# Revit family: Hager-Orion_Plus-IP65-D160-Cl.I-Steel_encl-630A-CH-de
name_source: partatom
category: Electrical Equipment
units: mm (PartAtom-declared; Revit-internal decimal feet)

## family parameters
Cut with Voids When Loaded = No
Host = Face
Panel Configuration = Two Columns, Circuits Across
Part Type = Panelboard
Room Calculation Point = No
Round Connector Dimension = Use Diameter
Shared = No

## types (14) — shared parameters
EF000003 - Montageart = EV000384 - Aufputz
EF000007 - Farbe = EV000270 - grau
EF000049 - Tiefe = 160 mm  [stored 0.524934 ft]
EF000116 - RAL-Nummer = 7035
EF000118 - Mit Montageplatte = No
EF000437 - Anzahl der Leitungseinführungen = 2
EF001596 - Werkstoff des Gehäuses = EV000179 - Stahl
EF001613 - Funktionserhalt = EV000494 - ohne
EF003532 - Geeignet für Außengebrauch = No
EF004293 - Schlagfestigkeit = EV008784 - IK10
EF004464 - Art der Tür = EV002646 - Einzel
EF005474 - Schutzart (IP) = EV006421 - IP65
EF006306 - Mit Schloss = Yes
EF007800 - Geeignet für Blitzschutz = No
EF008873 - Nennstrom (In) = 630 A
EF009171 - Materialstärke Tür/Deckel = 2 mm  [stored 0.00656168 ft]
EF009554 - Anzahl der Öffnungen für Flanschplatten = 2
EF015940 - Deckel mit Überdruckentlastung = No
HG000002 - Mit tür = Yes
HG000003 - Bereich = Orion Plus
HG000006 - Unterputz = No
HG000009 - Doppelflügeligen Tür = No
HG000010 - Asymmetrische Türen = No
HG000023 - Gehäuse mit doppeltem Querschnitt = No
HG000024 - Höhe des unteren Teils = 800 mm
HG000026 - Stehend auf dem Boden = No
Manufacturer = Hager
Type Comments = Orion Plus
zero-valued in all types: Default Elevation, EF000218 - Einbautiefe, HG000027 - Sockelhöhe

## per-type parameters (varying)
| type | EF000008 - Breite | EF000040 - Höhe | EF000266 - Anzahl der Reihen | EF000339 - Art der Abdeckung | EF001088 - Anbaumöglichkeit | EF001131 - Innentiefe | EF002950 - Breite in Teilungseinheiten | EF004427 - Anzahl der Module | EF006244 - Transparenter Deckel/Tür | EF009170 - Materialstärke Gehäuse | EF009212 - Ausführung Deckel | HG000004 - Herstellerreferenz |
| Aufputz IP65 B200 H250 T160  - FL101A | 200 mm  [stored 0.656168 ft] | 250 mm  [stored 0.82021 ft] | 0 | EV004216 - Tür | No | 160 mm  [stored 0.524934 ft] | 0 | 0 | No | 2 mm  [stored 0.00656168 ft] | EV009916 - mit Ausschnitt | FL101A |
| Aufputz IP65 B200 H250 T160  - FL151A | 200 mm  [stored 0.656168 ft] | 250 mm  [stored 0.82021 ft] | 0 | EV004216 - Tür | No | 160 mm  [stored 0.524934 ft] | 0 | 0 | Yes | 2 mm  [stored 0.00656168 ft] | EV009916 - mit Ausschnitt | FL151A |
| Aufputz IP65 B250 H300 T160  - FL102A | 250 mm  [stored 0.82021 ft] | 300 mm | 1 | EV004216 - Tür | Yes | 160 mm  [stored 0.524934 ft] | 0 | 0 | No | 2 mm  [stored 0.00656168 ft] | EV009916 - mit Ausschnitt | FL102A |
| Aufputz IP65 B250 H300 T160  - FL152A | 250 mm  [stored 0.82021 ft] | 300 mm | 0 | EV004216 - Tür | Yes | 160 mm  [stored 0.524934 ft] | 0 | 0 | Yes | 1 mm  [stored 0.00328084 ft] | EV000116 - geschlossen | FL152A |
| Aufputz IP65 B300 H300 T160  - FL103A | 300 mm | 300 mm | 0 | EV004216 - Tür | No | 160 mm  [stored 0.524934 ft] | 0 | 0 | No | 2 mm  [stored 0.00656168 ft] | EV009916 - mit Ausschnitt | FL103A |
| Aufputz IP65 B300 H300 T160  - FL153A | 300 mm | 300 mm | 0 | EV004216 - Tür | Yes | 155 mm | 0 | 0 | Yes | 2 mm  [stored 0.00656168 ft] | EV009916 - mit Ausschnitt | FL153A |
| Aufputz IP65 B300 H350 T160  - FL104A | 300 mm | 350 mm  [stored 1.14829 ft] | 2 | EV001012 - Deckel | Yes | 160 mm  [stored 0.524934 ft] | 10 | 20 | No | 2 mm  [stored 0.00656168 ft] | EV000116 - geschlossen | FL104A |
| Aufputz IP65 B300 H350 T160  - FL154A | 300 mm | 350 mm  [stored 1.14829 ft] | 2 | EV004216 - Tür | Yes | 160 mm  [stored 0.524934 ft] | 10 | 20 | Yes | 1 mm  [stored 0.00328084 ft] | EV000116 - geschlossen | FL154A |
| Aufputz IP65 B300 H400 T160  - FL106A | 300 mm | 400 mm  [stored 1.31234 ft] | 0 | EV004216 - Tür | No | 160 mm  [stored 0.524934 ft] | 0 | 0 | No | 2 mm  [stored 0.00656168 ft] | EV009916 - mit Ausschnitt | FL106A |
| Aufputz IP65 B300 H400 T160  - FL156A | 300 mm | 400 mm  [stored 1.31234 ft] | 0 | EV004216 - Tür | No | 160 mm  [stored 0.524934 ft] | 0 | 0 | Yes | 2 mm  [stored 0.00656168 ft] | EV009916 - mit Ausschnitt | FL156A |
| Aufputz IP65 B300 H500 T160  - FL109A | 300 mm | 500 mm  [stored 1.64042 ft] | 3 | EV004216 - Tür | Yes | 160 mm  [stored 0.524934 ft] | 10 | 30 | No | 1 mm  [stored 0.00328084 ft] | EV000116 - geschlossen | FL109A |
| Aufputz IP65 B300 H500 T160  - FL159A | 300 mm | 500 mm  [stored 1.64042 ft] | 3 | EV004216 - Tür | Yes | 160 mm  [stored 0.524934 ft] | 10 | 30 | Yes | 1 mm  [stored 0.00328084 ft] | EV000116 - geschlossen | FL159A |
| Aufputz IP65 B400 H500 T160  - FL111A | 400 mm  [stored 1.31234 ft] | 500 mm  [stored 1.64042 ft] | 3 | EV004216 - Tür | Yes | 160 mm  [stored 0.524934 ft] | 16 | 54 | No | 1 mm  [stored 0.00328084 ft] | EV000116 - geschlossen | FL111A |
| Aufputz IP65 B400 H500 T160  - FL161A | 400 mm  [stored 1.31234 ft] | 500 mm  [stored 1.64042 ft] | 3 | EV004216 - Tür | Yes | 160 mm  [stored 0.524934 ft] | 16 | 54 | Yes | 1 mm  [stored 0.00328084 ft] | EV000116 - geschlossen | FL161A |

note: [stored X ft] marks values corroborated as IEEE doubles in the binary element streams (Revit-internal decimal feet)

## geometry (parser evidence)
native form markers: Sweep x7
no freeform markers — native parametric forms only
